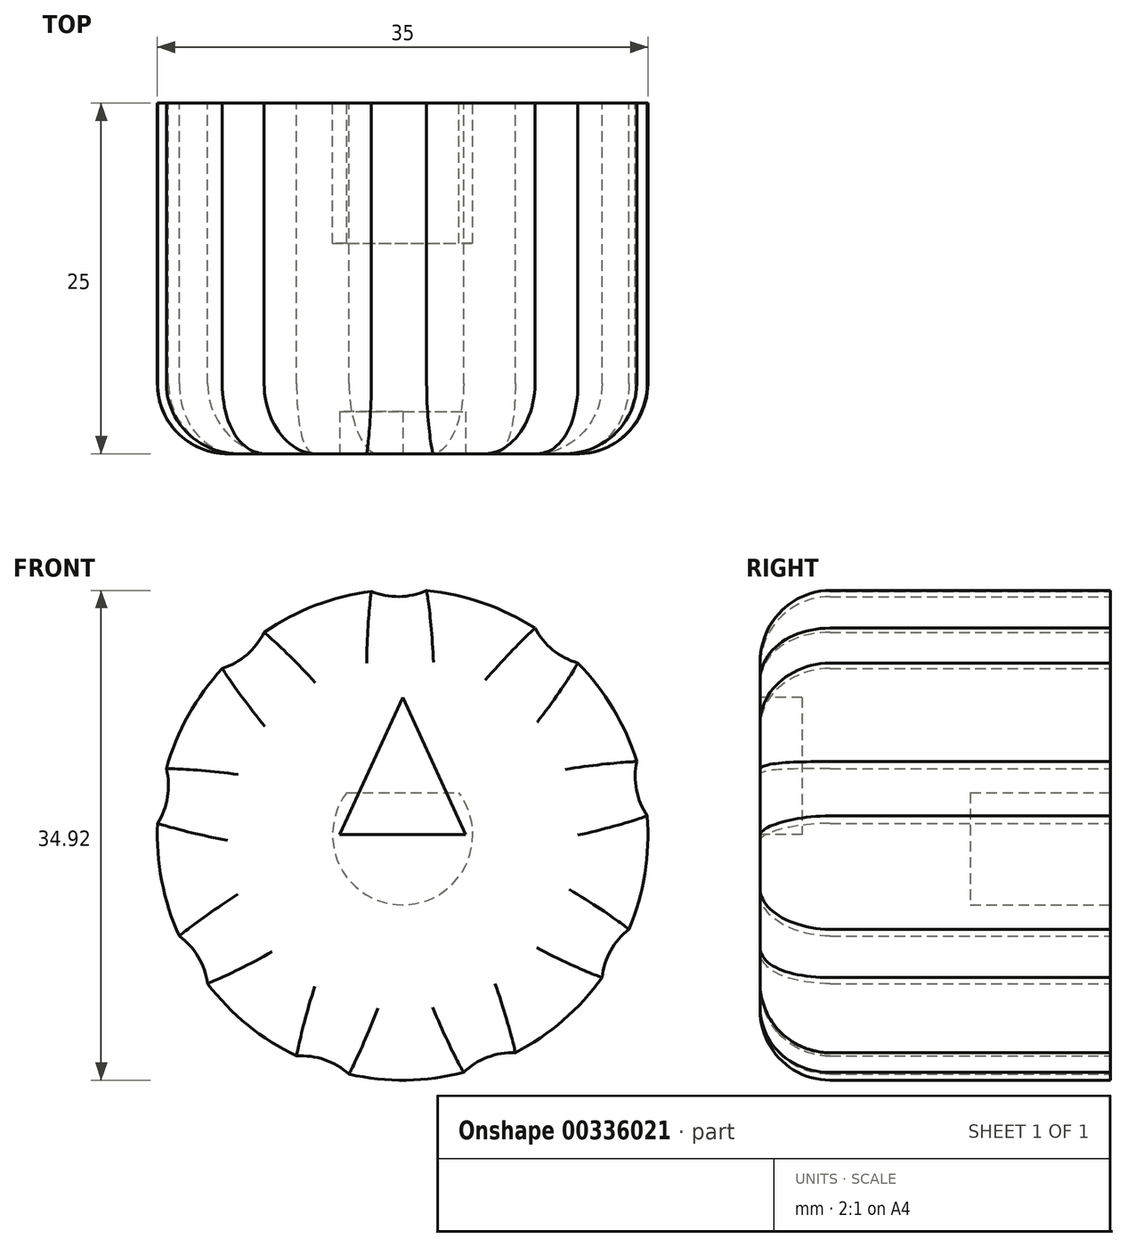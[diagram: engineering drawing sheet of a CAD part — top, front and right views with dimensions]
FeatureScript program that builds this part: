
annotation { "Feature Type Name" : "Feature", "Feature Type Description" : "" }
export const myFeature = defineFeature(function(context is Context, id is Id, definition is map)
    precondition{}
    {
        {
            var Q0;
            Q0=qCreatedBy(makeId("Front.planeOp"),FACE);
            var sketch = newSketch(context, id + "F0", { "sketchPlane" : qUnion([Q0])});
            skCircle(sketch, "E0", {"center": v(0, 0) * mm, "radius": 17.5 * mm});
            skCircle(sketch, "E1", {"center": v(0, 0) * mm, "radius": 5 * mm});
            skLineSegment(sketch, "E2", {"start": v(-4, 3) * mm, "end": v(4, 3) * mm});
            skLineSegment(sketch, "E3", {"start": v(-2.24, 17.36) * mm, "end": v(1.71, 17.42) * mm, "construction": true});
            skArc(sketch, "E4", {"start": v(-2.24, 17.36) * mm, "mid": v(-0.26, 16.98) * mm, "end": v(1.71, 17.42) * mm});
            skArc(sketch, "E5.1.0", {"start": v(-12.87, 11.86) * mm, "mid": v(-11.11, 12.84) * mm, "end": v(-9.88, 14.44) * mm});
            skArc(sketch, "E5.2.0", {"start": v(-17.48, 0.81) * mm, "mid": v(-16.77, 2.7) * mm, "end": v(-16.85, 4.7) * mm});
            skArc(sketch, "E5.3.0", {"start": v(-13.91, -10.61) * mm, "mid": v(-14.58, -8.71) * mm, "end": v(-15.94, -7.23) * mm});
            skArc(sketch, "E5.4.0", {"start": v(-3.84, -17.07) * mm, "mid": v(-5.57, -16.04) * mm, "end": v(-7.56, -15.78) * mm});
            skArc(sketch, "E5.5.0", {"start": v(8.04, -15.55) * mm, "mid": v(6.05, -15.87) * mm, "end": v(4.35, -16.95) * mm});
            skArc(sketch, "E5.6.0", {"start": v(16.15, -6.74) * mm, "mid": v(14.83, -8.27) * mm, "end": v(14.23, -10.19) * mm});
            skArc(sketch, "E5.7.0", {"start": v(16.7, 5.22) * mm, "mid": v(16.68, 3.2) * mm, "end": v(17.45, 1.34) * mm});
            skArc(sketch, "E5.8.0", {"start": v(9.44, 14.73) * mm, "mid": v(10.72, 13.17) * mm, "end": v(12.5, 12.24) * mm});
            skSolve(sketch);
        }
        {
            var Q0;
            {var subQ8=sQuery(id+"F0.wireOp",EDGE,"E4");Q0=makeQuery(id+"F0.imprint","IMPRINT",FACE,{"disambiguationData":[TD([[makeQuery(id+"F0.imprint","IMPRINT",EDGE,{"derivedFrom":subQ8}),-1.0]])]});}
            var Q1;
            {var subQ0=sQuery(id+"F0.wireOp",EDGE,"E2");Q1=makeQuery(id+"F0.imprint","IMPRINT",FACE,{"disambiguationData":[TD([[makeQuery(id+"F0.imprint","IMPRINT",EDGE,{"derivedFrom":subQ0}),1.0]])]});}
            var Q2;
            {var subQ0=sQuery(id+"F0.wireOp",EDGE,"E2");Q2=makeQuery(id+"F0.imprint","IMPRINT",FACE,{"disambiguationData":[TD([[makeQuery(id+"F0.imprint","IMPRINT",EDGE,{"derivedFrom":subQ0}),-1.0]])]});}
            extrude(context, id + "F1", {"entities" : qUnion([Q0, Q1, Q2]), "depth" : 25 * mm});
        }
        {
            var Q0;
            {var subQ0=sQuery(id+"F0.wireOp",EDGE,"E2");Q0=makeQuery(id+"F0.imprint","IMPRINT",FACE,{"disambiguationData":[TD([[makeQuery(id+"F0.imprint","IMPRINT",EDGE,{"derivedFrom":subQ0}),-1.0]])]});}
            extrude(context, id + "F2", {"entities" : qUnion([Q0]), "operationType" : NewBodyOperationType.REMOVE, "depth" : 10 * mm});
        }
        {
            var Q0;
            Q0=makeQuery(id+"F1.opExtrude","CAP_FACE",FACE,{"disambiguationData":[OSD([sQuery(id+"F0.wireOp",EDGE,"E0"),sQuery(id+"F0.wireOp",EDGE,"E4"),sQuery(id+"F0.wireOp",EDGE,"E5.1.0"),sQuery(id+"F0.wireOp",EDGE,"E5.2.0"),sQuery(id+"F0.wireOp",EDGE,"E5.3.0"),sQuery(id+"F0.wireOp",EDGE,"E5.4.0"),sQuery(id+"F0.wireOp",EDGE,"E5.5.0"),sQuery(id+"F0.wireOp",EDGE,"E5.6.0"),sQuery(id+"F0.wireOp",EDGE,"E5.7.0"),sQuery(id+"F0.wireOp",EDGE,"E5.8.0")])],"isStart":false});
            fillet(context, id + "F3", {"entities" : qUnion([Q0]), "radius" : 5 * mm, "tangentPropagation" : true, "allowEdgeOverflow" : false});
        }
        {
            var Q0;
            Q0=makeQuery(id+"F1.opExtrude","CAP_FACE",FACE,{"disambiguationData":[OSD([sQuery(id+"F0.wireOp",EDGE,"E0"),sQuery(id+"F0.wireOp",EDGE,"E4"),sQuery(id+"F0.wireOp",EDGE,"E5.1.0"),sQuery(id+"F0.wireOp",EDGE,"E5.2.0"),sQuery(id+"F0.wireOp",EDGE,"E5.3.0"),sQuery(id+"F0.wireOp",EDGE,"E5.4.0"),sQuery(id+"F0.wireOp",EDGE,"E5.5.0"),sQuery(id+"F0.wireOp",EDGE,"E5.6.0"),sQuery(id+"F0.wireOp",EDGE,"E5.7.0"),sQuery(id+"F0.wireOp",EDGE,"E5.8.0")])],"isStart":false});
            var sketch = newSketch(context, id + "F4", { "sketchPlane" : qUnion([Q0])});
            skLineSegment(sketch, "E6", {"start": v(0, 11.05) * mm, "end": v(0, -6.3) * mm, "construction": true});
            skLineSegment(sketch, "E7", {"start": v(0, 9.8) * mm, "end": v(4.5, 0) * mm});
            skLineSegment(sketch, "E8", {"start": v(4.5, 0) * mm, "end": v(0, 0) * mm});
            skLineSegment(sketch, "E9.MirrorCS", {"start": v(0, 9.8) * mm, "end": v(-4.5, 0) * mm});
            skLineSegment(sketch, "E10.MirrorCS", {"start": v(-4.5, 0) * mm, "end": v(0, 0) * mm});
            skSolve(sketch);
        }
        {
            var Q0;
            Q0=makeQuery(id+"F4.imprint","IMPRINT",FACE,{"disambiguationData":[TD([[makeQuery(id+"F4.imprint","IMPRINT",EDGE,{"derivedFrom":sQuery(id+"F4.wireOp",EDGE,"E7")}),-1.0]])]});
            extrude(context, id + "F5", {"entities" : qUnion([Q0]), "operationType" : NewBodyOperationType.REMOVE, "oppositeDirection" : true, "depth" : 3 * mm});
        }
    });
